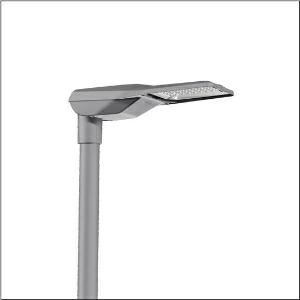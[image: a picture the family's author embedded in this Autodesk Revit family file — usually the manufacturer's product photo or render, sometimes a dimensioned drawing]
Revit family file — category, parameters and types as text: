
# Revit family: streetlight_sl_21_iq_mini___st0_5a_5xe2b31d08hb_2e1a
name_source: partatom
category: Lighting Fixtures
units: mm (PartAtom-declared; Revit-internal decimal feet)

## family parameters
Cut with Voids When Loaded = No
Host = Face
Light Source = No
Part Type = Normal
Room Calculation Point = No
Round Connector Dimension = Use Diameter
Shared = No

## types (1)
- --- (1 x LED, 9450 lm, 70.9 W, 3000K)
    Apparent Load = 71 VA
    CIE Flux Codes = 41 75 97 100 100
    Color Rendering = 70
    Color Temperature = 3000K
    Default Elevation = 1800 mm
    Description = Streetlight SL 21 iQ mini, mast luminaire, primary light control with lens, of PMMA, primary optical cover: cover, of toughened safety glass, transparent, light distribution: ST0.5a, light emission: direct distribution, primary light characteristic: asymmetric, installation type: post-top, side-entry, LED, High Power LED, rated luminous flux: 9.450lm, luminous efficacy: 133lm/W, light colour: 730, colour temperature: 3000K, control: Auto-Match, Temp-Guard, Lumen-Switch, Night-Set, Smart-Wire, Light-Fading, Desk-Remote (wireless, voltage-free reading and setting of iQ features in the workshop via application-optimized NFC function/RFID function), optimised constant luminous flux control (CLO 2.0), presetting dimming linear, mains connection: 220..240V, AC, 50/60Hz, start of lifetime: 71W, end of service life: 75W, reduction: 31W, luminaire housing, of diecast aluminium, powder-coated, Siteco® metallic grey (DB 702S), corrosivity category C5 mid according to DIN EN ISO 12944, please order mast flange separately, inclination adjustable: 0°, 5°, 10°, 15°, sealing non-destructively replaceable, multi-level sealing system, length: 628mm, width: 235mm, height: 110mm, mast flange for spigot size: 42mm (side-entry): 5XC10008XM4, 60/48mm (side-entry/post-top): 5XC10108XM2, 76/60mm (side-entry/post-top): 5XC10108XM1, protection rating (complete): IP66, insulation class (complete): insulation class II (safety insulation), certification: CE, ENEC, ENEC+, VDE, impact resistance: IK09, permissible operating ambient temperature for outdoor applications: -40..+50°C, standard-compliant lighting for roads and squares, packaging unit: 1 piece

Light Distribution: ST0.5a
    Height = 110 mm
    Lamp = 1 x LED
    Lamp Light Flux = 9450 lm
    Lamp Power = 70.9 W
    Lamp count = 1
    Length = 625 mm
    Luminous efficacy = 133 lm/W
    Manufacturer = Siteco
    ModVariant = No
    Model = 5XE2B31D08HB
    Number of Poles = 1
    OnlyDefault = Yes
    Power Factor = 1
    Product Name = Streetlight SL 21 iQ mini | ST0.5a
    Product group = mast luminaire | pylon top
    ProductGroupID = 6100
    Protection Class = Protection class II
    Protection Degree = IP 66
    RLX_Detail_Level = 1
    RLX_Emergency_Light_Flux = 0 lm
    RLX_Emergency_Type = 0
    RLX_Emergency_Type_DB = No
    RlxData = <blob elided: 103529 chars, md5=1277791a>
    Socket = socket
    Standby Power = 0 W
    System Light Flux = 9450 lm
    System Power = 71 W
    Type Comments = factory setting: luminous flux: 100 % | dim-lin: 254 | 711 mA
    Type Image = l_1003519.jpg
    URL = http://relux.com
    VarID = @adj_108803
    Voltage = 0 V
    Weight = 0.00 kg
    Width = 234 mm

## geometry (parser evidence)
native form markers: Blend x4, Sweep x10
no freeform markers — native parametric forms only
